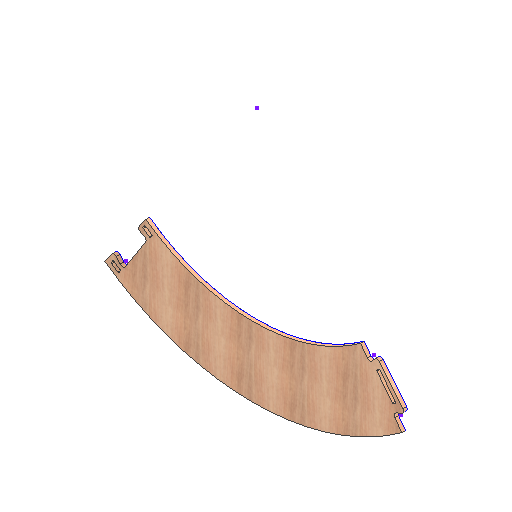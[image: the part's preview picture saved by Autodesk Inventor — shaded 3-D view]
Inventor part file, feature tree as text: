
AUTODESK INVENTOR PART (.ipt)
format: ipt  version: 2021 (Build 250183000, 183)  size: 262,144 bytes
history: native  units: mm
features: other x2, extrude x2, hole x1
ambient origin geometry x8: Origin, YZ Plane, XZ Plane, XY Plane, X Axis, Y Axis, Z Axis, Center Point
bodies: Solid1 (feature_tree)
feature tree (5):
  other  "CONTOURS"
  hole  "HOLES"  [1 undecoded]
  other  "LETTERS"
  extrude  "Extrusion2"  Depth=18.0mm TaperAngle=0.0deg
  extrude  "Extrusion3"  [1 undecoded]
note: 2 required parameter values undecoded (feature->parameter linkage not recoverable at this tier; creation-order binding heuristic only, values carry confidence <= 0.55)
